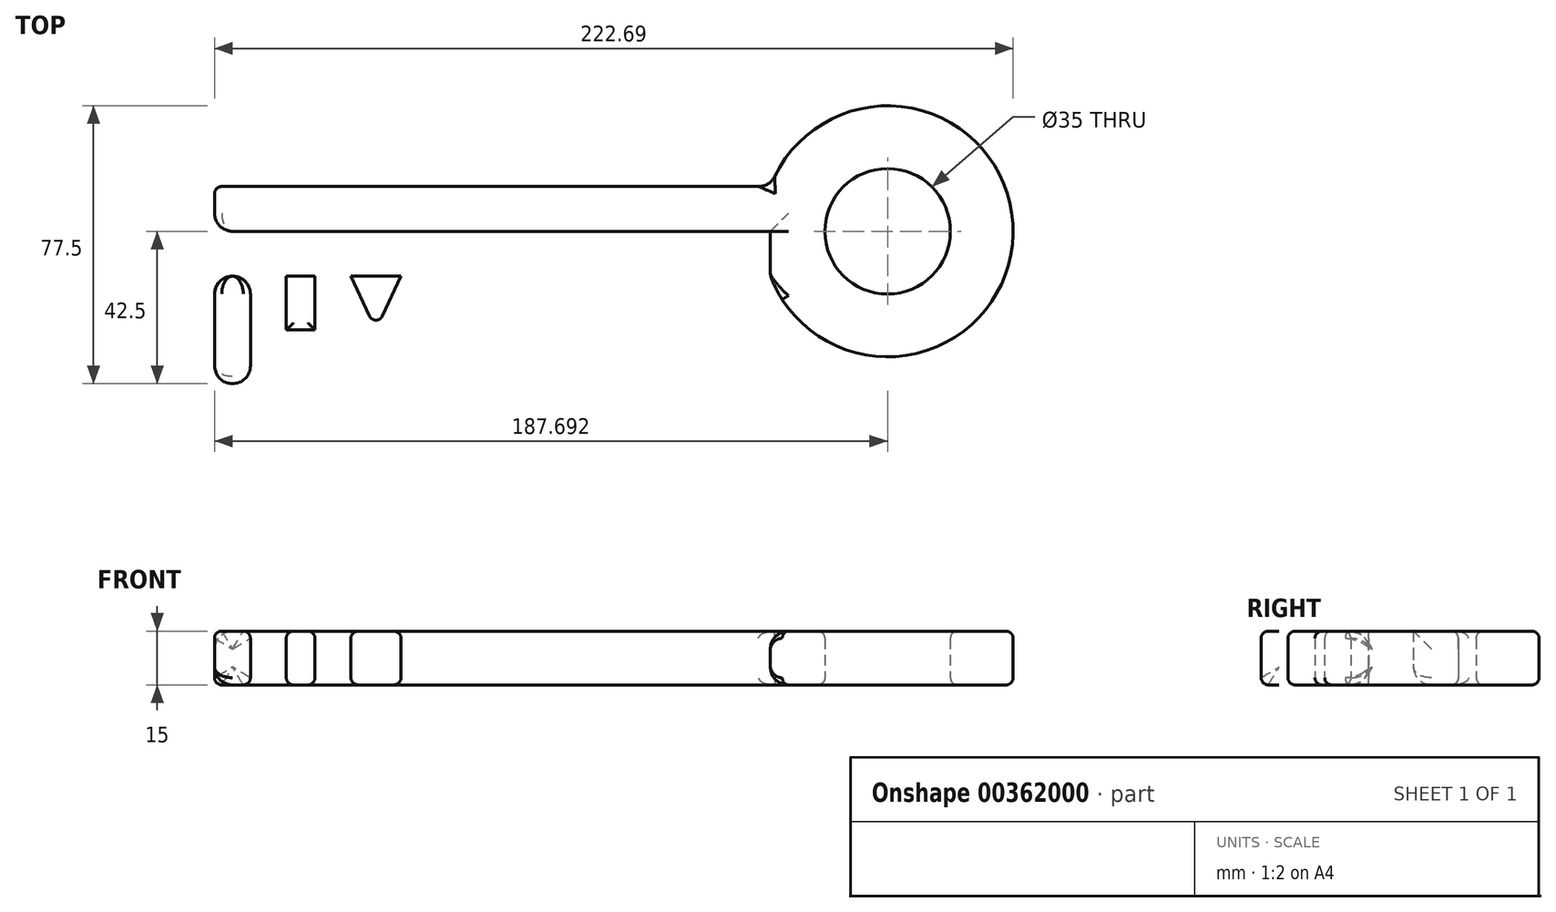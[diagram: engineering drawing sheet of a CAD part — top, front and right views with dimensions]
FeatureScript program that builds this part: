
annotation { "Feature Type Name" : "Feature", "Feature Type Description" : "" }
export const myFeature = defineFeature(function(context is Context, id is Id, definition is map)
    precondition{}
    {
        {
            var Q0;
            Q0=qCreatedBy(makeId("Top.planeOp"),FACE);
            var sketch = newSketch(context, id + "F0", { "sketchPlane" : qUnion([Q0])});
            skLineSegment(sketch, "E0.bottom", {"start": v(-105.84, 55) * mm, "end": v(49.16, 55) * mm});
            skLineSegment(sketch, "E0.top", {"start": v(-105.84, 30) * mm, "end": v(49.16, 30) * mm});
            skLineSegment(sketch, "E0.left", {"start": v(-105.84, 55) * mm, "end": v(-105.84, 30) * mm});
            skLineSegment(sketch, "E0.right", {"start": v(49.16, 55) * mm, "end": v(49.16, 30) * mm});
            skLineSegment(sketch, "E1.bottom", {"start": v(50.65, 30) * mm, "end": v(-105.84, 30) * mm});
            skLineSegment(sketch, "E1.top", {"start": v(50.65, 30) * mm, "end": v(-105.84, 30) * mm});
            skLineSegment(sketch, "E1.left", {"start": v(50.65, 30) * mm, "end": v(50.65, 30) * mm});
            skLineSegment(sketch, "E1.right", {"start": v(-105.84, 30) * mm, "end": v(-105.84, 30) * mm});
            skLineSegment(sketch, "E2.bottom", {"start": v(-105.84, 0) * mm, "end": v(-95.84, 0) * mm});
            skLineSegment(sketch, "E2.top", {"start": v(-105.84, 30) * mm, "end": v(-95.84, 30) * mm});
            skLineSegment(sketch, "E2.left", {"start": v(-105.84, 0) * mm, "end": v(-105.84, 30) * mm});
            skLineSegment(sketch, "E2.right", {"start": v(-95.84, 0) * mm, "end": v(-95.84, 30) * mm});
            skPoint(sketch, "E3.firstSnap0", {"position": v(-95.84, 15) * mm});
            skLineSegment(sketch, "E3.bottom", {"start": v(-85.84, 15) * mm, "end": v(-77.84, 15) * mm});
            skLineSegment(sketch, "E3.top", {"start": v(-85.84, 30) * mm, "end": v(-77.84, 30) * mm});
            skLineSegment(sketch, "E3.left", {"start": v(-85.84, 15) * mm, "end": v(-85.84, 30) * mm});
            skLineSegment(sketch, "E3.right", {"start": v(-77.84, 15) * mm, "end": v(-77.84, 30) * mm});
            skLineSegment(sketch, "E4", {"start": v(-67.84, 30) * mm, "end": v(-60.84, 15) * mm});
            skLineSegment(sketch, "E5", {"start": v(-60.84, 15) * mm, "end": v(-53.84, 30) * mm});
            skArc(sketch, "E6", {"start": v(49.16, 30) * mm, "mid": v(116.85, 42.5) * mm, "end": v(49.16, 55) * mm});
            skCircle(sketch, "E7", {"center": v(81.85, 42.5) * mm, "radius": 17.5 * mm});
            skLineSegment(sketch, "E8", {"start": v(81.85, 42.5) * mm, "end": v(-105.84, 42.5) * mm});
            skLineSegment(sketch, "E9", {"start": v(33.31, 42.5) * mm, "end": v(-105.84, 42.5) * mm});
            skSolve(sketch);
        }
        {
            var Q0;
            {var subQ0=sQuery(id+"F0.wireOp",EDGE,"E4");Q0=makeQuery(id+"F0.imprint","IMPRINT",FACE,{"disambiguationData":[TD([[makeQuery(id+"F0.imprint","IMPRINT",EDGE,{"derivedFrom":subQ0}),1.0]])]});}
            var Q1;
            Q1=makeQuery(id+"F0.imprint","IMPRINT",FACE,{"disambiguationData":[TD([[makeQuery(id+"F0.imprint","IMPRINT",EDGE,{"derivedFrom":sQuery(id+"F0.wireOp",EDGE,"E2.bottom")}),1.0]])]});
            var Q2;
            Q2=makeQuery(id+"F0.imprint","IMPRINT",FACE,{"disambiguationData":[TD([[makeQuery(id+"F0.imprint","IMPRINT",EDGE,{"derivedFrom":sQuery(id+"F0.wireOp",EDGE,"E3.bottom")}),1.0]])]});
            var Q3;
            {var subQ0=sQuery(id+"F0.wireOp",EDGE,"E6");Q3=makeQuery(id+"F0.imprint","IMPRINT",FACE,{"disambiguationData":[TD([[makeQuery(id+"F0.imprint","IMPRINT",EDGE,{"derivedFrom":subQ0}),1.0]])]});}
            var Q4;
            {var subQ7=sQuery(id+"F0.wireOp",EDGE,"E3.top");Q4=makeQuery(id+"F0.imprint","IMPRINT",FACE,{"disambiguationData":[TD([[makeQuery(id+"F0.imprint","IMPRINT",EDGE,{"derivedFrom":subQ7}),1.0]])]});}
            var Q5;
            {var subQ4=sQuery(id+"F0.wireOp",EDGE,"E0.bottom");Q5=makeQuery(id+"F0.imprint","IMPRINT",FACE,{"disambiguationData":[TD([[makeQuery(id+"F0.imprint","IMPRINT",EDGE,{"derivedFrom":subQ4}),-1.0]])]});}
            extrude(context, id + "F1", {"entities" : qUnion([Q0, Q1, Q2, Q3, Q4, Q5]), "depth" : 15 * mm});
        }
        {
            var Q0;
            Q0=makeQuery(id+"F1.opExtrude","CAP_EDGE",EDGE,{"disambiguationData":[OSD([sQuery(id+"F0.wireOp",EDGE,"E0.bottom")])],"isStart":false});
            var Q1;
            Q1=makeQuery(id+"F1.opExtrude","CAP_EDGE",EDGE,{"disambiguationData":[OSD([sQuery(id+"F0.wireOp",EDGE,"E2.bottom")])],"isStart":false});
            var Q2;
            Q2=makeQuery(id+"F1.opExtrude","CAP_EDGE",EDGE,{"disambiguationData":[OSD([sQuery(id+"F0.wireOp",EDGE,"E2.left")])],"isStart":false});
            var Q3;
            {var subQ0=sQuery(id+"F0.wireOp",EDGE,"E1.top");Q3=makeQuery(id+"F1.opExtrude","CAP_EDGE",EDGE,{"disambiguationData":[OSD([subQ0]),TDD([makeQuery(id+"F0.imprint","IMPRINT",EDGE,{"disambiguationData":[TD([[makeQuery(id+"F0.imprint","INTERSECT",VERTEX,{"derivedFrom":[subQ0,sQuery(id+"F0.wireOp",EDGE,"E2.top"),sQuery(id+"F0.wireOp",EDGE,"E2.right")]}),1.0]])],"derivedFrom":subQ0})])],"isStart":false});}
            var Q4;
            Q4=makeQuery(id+"F1.opExtrude","CAP_EDGE",EDGE,{"disambiguationData":[OSD([sQuery(id+"F0.wireOp",EDGE,"E2.right")])],"isStart":false});
            var Q5;
            Q5=makeQuery(id+"F1.opExtrude","CAP_EDGE",EDGE,{"disambiguationData":[OSD([sQuery(id+"F0.wireOp",EDGE,"E3.left")])],"isStart":false});
            var Q6;
            Q6=makeQuery(id+"F1.opExtrude","CAP_EDGE",EDGE,{"disambiguationData":[OSD([sQuery(id+"F0.wireOp",EDGE,"E3.bottom")])],"isStart":false});
            var Q7;
            Q7=makeQuery(id+"F1.opExtrude","CAP_EDGE",EDGE,{"disambiguationData":[OSD([sQuery(id+"F0.wireOp",EDGE,"E3.right")])],"isStart":false});
            var Q8;
            {var subQ0=sQuery(id+"F0.wireOp",EDGE,"E1.top");Q8=makeQuery(id+"F1.opExtrude","CAP_EDGE",EDGE,{"disambiguationData":[OSD([subQ0]),TDD([makeQuery(id+"F0.imprint","IMPRINT",EDGE,{"disambiguationData":[TD([[makeQuery(id+"F0.imprint","INTERSECT",VERTEX,{"derivedFrom":[subQ0,sQuery(id+"F0.wireOp",EDGE,"E4")]}),-1.0]])],"derivedFrom":subQ0})])],"isStart":false});}
            var Q9;
            Q9=makeQuery(id+"F1.opExtrude","CAP_EDGE",EDGE,{"disambiguationData":[OSD([sQuery(id+"F0.wireOp",EDGE,"E4")])],"isStart":false});
            var Q10;
            {var subQ0=sQuery(id+"F0.wireOp",EDGE,"E1.top");Q10=makeQuery(id+"F1.opExtrude","CAP_EDGE",EDGE,{"disambiguationData":[OSD([subQ0]),TDD([makeQuery(id+"F0.imprint","IMPRINT",EDGE,{"disambiguationData":[TD([[makeQuery(id+"F0.imprint","INTERSECT",VERTEX,{"derivedFrom":[subQ0,sQuery(id+"F0.wireOp",EDGE,"E5")]}),1.0]])],"derivedFrom":subQ0})])],"isStart":false});}
            var Q11;
            Q11=makeQuery(id+"F1.opExtrude","CAP_EDGE",EDGE,{"disambiguationData":[OSD([sQuery(id+"F0.wireOp",EDGE,"E6")])],"isStart":false});
            var Q12;
            Q12=makeQuery(id+"F1.opExtrude","CAP_EDGE",EDGE,{"disambiguationData":[OSD([sQuery(id+"F0.wireOp",EDGE,"E7")])],"isStart":false});
            var Q13;
            Q13=makeQuery(id+"F1.opExtrude","CAP_EDGE",EDGE,{"disambiguationData":[OSD([sQuery(id+"F0.wireOp",EDGE,"E5")])],"isStart":true});
            var Q14;
            Q14=makeQuery(id+"F1.opExtrude","CAP_EDGE",EDGE,{"disambiguationData":[OSD([sQuery(id+"F0.wireOp",EDGE,"E0.left")])],"isStart":true});
            var Q15;
            Q15=makeQuery(id+"F1.opExtrude","CAP_EDGE",EDGE,{"disambiguationData":[OSD([sQuery(id+"F0.wireOp",EDGE,"E6")])],"isStart":true});
            var Q16;
            {var subQ0=sQuery(id+"F0.wireOp",EDGE,"E1.top");Q16=makeQuery(id+"F1.opExtrude","CAP_EDGE",EDGE,{"disambiguationData":[OSD([subQ0]),TDD([makeQuery(id+"F0.imprint","IMPRINT",EDGE,{"disambiguationData":[TD([[makeQuery(id+"F0.imprint","INTERSECT",VERTEX,{"derivedFrom":[subQ0,sQuery(id+"F0.wireOp",EDGE,"E5")]}),1.0]])],"derivedFrom":subQ0})])],"isStart":true});}
            var Q17;
            Q17=makeQuery(id+"F1.opExtrude","CAP_EDGE",EDGE,{"disambiguationData":[OSD([sQuery(id+"F0.wireOp",EDGE,"E3.bottom")])],"isStart":true});
            var Q18;
            Q18=makeQuery(id+"F1.opExtrude","CAP_EDGE",EDGE,{"disambiguationData":[OSD([sQuery(id+"F0.wireOp",EDGE,"E3.right")])],"isStart":true});
            var Q19;
            Q19=makeQuery(id+"F1.opExtrude","CAP_EDGE",EDGE,{"disambiguationData":[OSD([sQuery(id+"F0.wireOp",EDGE,"E2.right")])],"isStart":true});
            var Q20;
            Q20=makeQuery(id+"F1.opExtrude","CAP_EDGE",EDGE,{"disambiguationData":[OSD([sQuery(id+"F0.wireOp",EDGE,"E2.bottom")])],"isStart":true});
            var Q21;
            Q21=makeQuery(id+"F1.opExtrude","CAP_EDGE",EDGE,{"disambiguationData":[OSD([sQuery(id+"F0.wireOp",EDGE,"E7")])],"isStart":true});
            var Q22;
            Q22=makeQuery(id+"F1.opExtrude","CAP_EDGE",EDGE,{"disambiguationData":[OSD([sQuery(id+"F0.wireOp",EDGE,"E0.bottom")])],"isStart":true});
            var Q23;
            Q23=makeQuery(id+"F1.opExtrude","SWEPT_EDGE",EDGE,{"disambiguationData":[OSD([sQuery(id+"F0.wireOp",EDGE,"E0.bottom"),sQuery(id+"F0.wireOp",EDGE,"E0.left")])]});
            var Q24;
            Q24=makeQuery(id+"F1.opExtrude","CAP_EDGE",EDGE,{"disambiguationData":[OSD([sQuery(id+"F0.wireOp",EDGE,"E4")])],"isStart":true});
            var Q25;
            Q25=makeQuery(id+"F1.opExtrude","SWEPT_EDGE",EDGE,{"disambiguationData":[OSD([sQuery(id+"F0.wireOp",EDGE,"E4"),sQuery(id+"F0.wireOp",EDGE,"E5")])]});
            var Q26;
            Q26=makeQuery(id+"F1.opExtrude","CAP_EDGE",EDGE,{"disambiguationData":[OSD([sQuery(id+"F0.wireOp",EDGE,"E5")])],"isStart":false});
            var Q27;
            {var subQ0=sQuery(id+"F0.wireOp",EDGE,"E1.top");Q27=makeQuery(id+"F1.opExtrude","CAP_EDGE",EDGE,{"disambiguationData":[OSD([subQ0]),TDD([makeQuery(id+"F0.imprint","IMPRINT",EDGE,{"disambiguationData":[TD([[makeQuery(id+"F0.imprint","INTERSECT",VERTEX,{"derivedFrom":[subQ0,sQuery(id+"F0.wireOp",EDGE,"E2.top"),sQuery(id+"F0.wireOp",EDGE,"E2.right")]}),1.0]])],"derivedFrom":subQ0})])],"isStart":true});}
            var Q28;
            Q28=makeQuery(id+"F1.opExtrude","CAP_EDGE",EDGE,{"disambiguationData":[OSD([sQuery(id+"F0.wireOp",EDGE,"E3.left")])],"isStart":true});
            var Q29;
            {var subQ0=sQuery(id+"F0.wireOp",EDGE,"E1.top");Q29=makeQuery(id+"F1.opExtrude","CAP_EDGE",EDGE,{"disambiguationData":[OSD([subQ0]),TDD([makeQuery(id+"F0.imprint","IMPRINT",EDGE,{"disambiguationData":[TD([[makeQuery(id+"F0.imprint","INTERSECT",VERTEX,{"derivedFrom":[subQ0,sQuery(id+"F0.wireOp",EDGE,"E4")]}),-1.0]])],"derivedFrom":subQ0})])],"isStart":true});}
            fillet(context, id + "F2", {"entities" : qUnion([Q0, Q1, Q2, Q3, Q4, Q5, Q6, Q7, Q8, Q9, Q10, Q11, Q12, Q13, Q14, Q15, Q16, Q17, Q18, Q19, Q20, Q21, Q22, Q23, Q24, Q25, Q26, Q27, Q28, Q29]), "radius" : 2 * mm, "tangentPropagation" : true, "allowEdgeOverflow" : false});
        }
        {
            var Q0;
            Q0=makeQuery(id+"F1.opExtrude","CAP_EDGE",EDGE,{"disambiguationData":[OSD([sQuery(id+"F0.wireOp",EDGE,"E2.left")])],"isStart":true});
            var Q1;
            Q1=makeQuery(id+"F1.opExtrude","CAP_EDGE",EDGE,{"disambiguationData":[OSD([sQuery(id+"F0.wireOp",EDGE,"E2.right")])],"isStart":true});
            var Q2;
            {var subQ0=sQuery(id+"F0.wireOp",EDGE,"E1.top");Q2=makeQuery(id+"F1.opExtrude","CAP_EDGE",EDGE,{"disambiguationData":[OSD([subQ0]),TDD([makeQuery(id+"F0.imprint","IMPRINT",EDGE,{"disambiguationData":[TD([[makeQuery(id+"F0.imprint","INTERSECT",VERTEX,{"derivedFrom":[subQ0,sQuery(id+"F0.wireOp",EDGE,"E2.top"),sQuery(id+"F0.wireOp",EDGE,"E2.right")]}),1.0]])],"derivedFrom":subQ0})])],"isStart":true});}
            var Q3;
            Q3=makeQuery(id+"F1.opExtrude","CAP_EDGE",EDGE,{"disambiguationData":[OSD([sQuery(id+"F0.wireOp",EDGE,"E3.left")])],"isStart":true});
            var Q4;
            Q4=makeQuery(id+"F1.opExtrude","CAP_EDGE",EDGE,{"disambiguationData":[OSD([sQuery(id+"F0.wireOp",EDGE,"E3.bottom")])],"isStart":true});
            var Q5;
            Q5=makeQuery(id+"F1.opExtrude","CAP_EDGE",EDGE,{"disambiguationData":[OSD([sQuery(id+"F0.wireOp",EDGE,"E3.right")])],"isStart":true});
            var Q6;
            Q6=makeQuery(id+"F1.opExtrude","CAP_EDGE",EDGE,{"disambiguationData":[OSD([sQuery(id+"F0.wireOp",EDGE,"E2.bottom")])],"isStart":true});
            var Q7;
            {var subQ0=sQuery(id+"F0.wireOp",EDGE,"E1.top");Q7=makeQuery(id+"F1.opExtrude","CAP_EDGE",EDGE,{"disambiguationData":[OSD([subQ0]),TDD([makeQuery(id+"F0.imprint","IMPRINT",EDGE,{"disambiguationData":[TD([[makeQuery(id+"F0.imprint","INTERSECT",VERTEX,{"derivedFrom":[subQ0,sQuery(id+"F0.wireOp",EDGE,"E4")]}),-1.0]])],"derivedFrom":subQ0})])],"isStart":true});}
            var Q8;
            Q8=makeQuery(id+"F1.opExtrude","CAP_EDGE",EDGE,{"disambiguationData":[OSD([sQuery(id+"F0.wireOp",EDGE,"E4")])],"isStart":true});
            var Q9;
            {var subQ0=sQuery(id+"F0.wireOp",EDGE,"E1.top");Q9=makeQuery(id+"F1.opExtrude","CAP_EDGE",EDGE,{"disambiguationData":[OSD([subQ0]),TDD([makeQuery(id+"F0.imprint","IMPRINT",EDGE,{"disambiguationData":[TD([[makeQuery(id+"F0.imprint","INTERSECT",VERTEX,{"derivedFrom":[subQ0,sQuery(id+"F0.wireOp",EDGE,"E5")]}),1.0]])],"derivedFrom":subQ0})])],"isStart":true});}
            var Q10;
            {var subQ0=sQuery(id+"F0.wireOp",EDGE,"E5");Q10=makeQuery(id+"F2.opFillet","BLEND_EDGE",EDGE,{"blendedFrom":[makeQuery(id+"F1.opExtrude","CAP_EDGE",EDGE,{"disambiguationData":[OSD([subQ0])],"isStart":true}),makeQuery(id+"F1.opExtrude","CAP_FACE",FACE,{"disambiguationData":[OSD([sQuery(id+"F0.wireOp",EDGE,"E0.bottom"),sQuery(id+"F0.wireOp",EDGE,"E0.left"),sQuery(id+"F0.wireOp",EDGE,"E1.top"),sQuery(id+"F0.wireOp",EDGE,"E2.bottom"),sQuery(id+"F0.wireOp",EDGE,"E2.top"),sQuery(id+"F0.wireOp",EDGE,"E2.left"),sQuery(id+"F0.wireOp",EDGE,"E2.right"),sQuery(id+"F0.wireOp",EDGE,"E3.bottom"),sQuery(id+"F0.wireOp",EDGE,"E3.left"),sQuery(id+"F0.wireOp",EDGE,"E3.right"),sQuery(id+"F0.wireOp",EDGE,"E4"),subQ0,sQuery(id+"F0.wireOp",EDGE,"E6"),sQuery(id+"F0.wireOp",EDGE,"E7")])],"isStart":true})],"blendedInto":[makeQuery(id+"F1.opExtrude","CAP_FACE",FACE,{"disambiguationData":[OSD([sQuery(id+"F0.wireOp",EDGE,"E0.bottom"),sQuery(id+"F0.wireOp",EDGE,"E0.left"),sQuery(id+"F0.wireOp",EDGE,"E1.top"),sQuery(id+"F0.wireOp",EDGE,"E2.bottom"),sQuery(id+"F0.wireOp",EDGE,"E2.top"),sQuery(id+"F0.wireOp",EDGE,"E2.left"),sQuery(id+"F0.wireOp",EDGE,"E2.right"),sQuery(id+"F0.wireOp",EDGE,"E3.bottom"),sQuery(id+"F0.wireOp",EDGE,"E3.left"),sQuery(id+"F0.wireOp",EDGE,"E3.right"),sQuery(id+"F0.wireOp",EDGE,"E4"),subQ0,sQuery(id+"F0.wireOp",EDGE,"E6"),sQuery(id+"F0.wireOp",EDGE,"E7")])],"isStart":true})]});}
            var Q11;
            Q11=makeQuery(id+"F1.opExtrude","CAP_EDGE",EDGE,{"disambiguationData":[OSD([sQuery(id+"F0.wireOp",EDGE,"E6")])],"isStart":true});
            var Q12;
            Q12=makeQuery(id+"F1.opExtrude","CAP_EDGE",EDGE,{"disambiguationData":[OSD([sQuery(id+"F0.wireOp",EDGE,"E7")])],"isStart":true});
            var Q13;
            Q13=makeQuery(id+"F1.opExtrude","CAP_EDGE",EDGE,{"disambiguationData":[OSD([sQuery(id+"F0.wireOp",EDGE,"E0.bottom")])],"isStart":true});
            var Q14;
            Q14=makeQuery(id+"F1.opExtrude","CAP_FACE",FACE,{"disambiguationData":[OSD([sQuery(id+"F0.wireOp",EDGE,"E0.bottom"),sQuery(id+"F0.wireOp",EDGE,"E0.left"),sQuery(id+"F0.wireOp",EDGE,"E1.top"),sQuery(id+"F0.wireOp",EDGE,"E2.bottom"),sQuery(id+"F0.wireOp",EDGE,"E2.top"),sQuery(id+"F0.wireOp",EDGE,"E2.left"),sQuery(id+"F0.wireOp",EDGE,"E2.right"),sQuery(id+"F0.wireOp",EDGE,"E3.bottom"),sQuery(id+"F0.wireOp",EDGE,"E3.left"),sQuery(id+"F0.wireOp",EDGE,"E3.right"),sQuery(id+"F0.wireOp",EDGE,"E4"),sQuery(id+"F0.wireOp",EDGE,"E5"),sQuery(id+"F0.wireOp",EDGE,"E6"),sQuery(id+"F0.wireOp",EDGE,"E7")])],"isStart":true});
            var Q15;
            {var subQ0=sQuery(id+"F0.wireOp",EDGE,"E0.left");Q15=makeQuery(id+"F2.opFillet","BLEND_EDGE",EDGE,{"blendedFrom":[makeQuery(id+"F1.opExtrude","CAP_EDGE",EDGE,{"disambiguationData":[OSD([subQ0])],"isStart":true}),makeQuery(id+"F1.opExtrude","SWEPT_FACE",FACE,{"disambiguationData":[OSD([subQ0])]})],"blendedInto":[makeQuery(id+"F1.opExtrude","SWEPT_FACE",FACE,{"disambiguationData":[OSD([subQ0])]})]});}
            var Q16;
            Q16=makeQuery(id+"F1.opExtrude","SWEPT_FACE",FACE,{"disambiguationData":[OSD([sQuery(id+"F0.wireOp",EDGE,"E0.left")])]});
            var Q17;
            {var subQ0=sQuery(id+"F0.wireOp",EDGE,"E2.left");Q17=makeQuery(id+"F2.opFillet","BLEND_EDGE",EDGE,{"blendedFrom":[makeQuery(id+"F1.opExtrude","CAP_EDGE",EDGE,{"disambiguationData":[OSD([subQ0])],"isStart":false}),makeQuery(id+"F1.opExtrude","CAP_FACE",FACE,{"disambiguationData":[OSD([sQuery(id+"F0.wireOp",EDGE,"E0.bottom"),sQuery(id+"F0.wireOp",EDGE,"E0.left"),sQuery(id+"F0.wireOp",EDGE,"E1.top"),sQuery(id+"F0.wireOp",EDGE,"E2.bottom"),subQ0,sQuery(id+"F0.wireOp",EDGE,"E2.right"),sQuery(id+"F0.wireOp",EDGE,"E3.bottom"),sQuery(id+"F0.wireOp",EDGE,"E3.left"),sQuery(id+"F0.wireOp",EDGE,"E3.right"),sQuery(id+"F0.wireOp",EDGE,"E4"),sQuery(id+"F0.wireOp",EDGE,"E5"),sQuery(id+"F0.wireOp",EDGE,"E6"),sQuery(id+"F0.wireOp",EDGE,"E7")])],"isStart":false})],"blendedInto":[makeQuery(id+"F1.opExtrude","CAP_FACE",FACE,{"disambiguationData":[OSD([sQuery(id+"F0.wireOp",EDGE,"E0.bottom"),sQuery(id+"F0.wireOp",EDGE,"E0.left"),sQuery(id+"F0.wireOp",EDGE,"E1.top"),sQuery(id+"F0.wireOp",EDGE,"E2.bottom"),subQ0,sQuery(id+"F0.wireOp",EDGE,"E2.right"),sQuery(id+"F0.wireOp",EDGE,"E3.bottom"),sQuery(id+"F0.wireOp",EDGE,"E3.left"),sQuery(id+"F0.wireOp",EDGE,"E3.right"),sQuery(id+"F0.wireOp",EDGE,"E4"),sQuery(id+"F0.wireOp",EDGE,"E5"),sQuery(id+"F0.wireOp",EDGE,"E6"),sQuery(id+"F0.wireOp",EDGE,"E7")])],"isStart":false})]});}
            var Q18;
            {var subQ0=sQuery(id+"F0.wireOp",EDGE,"E2.left");Q18=makeQuery(id+"F2.opFillet","BLEND_EDGE",EDGE,{"blendedFrom":[makeQuery(id+"F1.opExtrude","CAP_EDGE",EDGE,{"disambiguationData":[OSD([subQ0])],"isStart":false}),makeQuery(id+"F1.opExtrude","SWEPT_FACE",FACE,{"disambiguationData":[OSD([subQ0])]})],"blendedInto":[makeQuery(id+"F1.opExtrude","SWEPT_FACE",FACE,{"disambiguationData":[OSD([subQ0])]})]});}
            var Q19;
            Q19=makeQuery(id+"F2.opFillet","BLEND_EDGE",EDGE,{"blendedFrom":[makeQuery(id+"F1.opExtrude","CAP_EDGE",EDGE,{"disambiguationData":[OSD([sQuery(id+"F0.wireOp",EDGE,"E0.bottom")])],"isStart":false}),makeQuery(id+"F1.opExtrude","CAP_EDGE",EDGE,{"disambiguationData":[OSD([sQuery(id+"F0.wireOp",EDGE,"E0.left"),sQuery(id+"F0.wireOp",EDGE,"E2.left")])],"isStart":false})],"blendedInto":[]});
            var Q20;
            {var subQ0=sQuery(id+"F0.wireOp",EDGE,"E4");Q20=makeQuery(id+"F2.opFillet","BLEND_EDGE",EDGE,{"blendedFrom":[makeQuery(id+"F1.opExtrude","CAP_EDGE",EDGE,{"disambiguationData":[OSD([subQ0])],"isStart":false}),makeQuery(id+"F1.opExtrude","SWEPT_FACE",FACE,{"disambiguationData":[OSD([subQ0])]})],"blendedInto":[makeQuery(id+"F1.opExtrude","SWEPT_FACE",FACE,{"disambiguationData":[OSD([subQ0])]})]});}
            var Q21;
            Q21=makeQuery(id+"F2.opFillet","BLEND_EDGE",EDGE,{"blendedFrom":[makeQuery(id+"F1.opExtrude","CAP_EDGE",EDGE,{"disambiguationData":[OSD([sQuery(id+"F0.wireOp",EDGE,"E4")])],"isStart":false}),makeQuery(id+"F1.opExtrude","SWEPT_FACE",FACE,{"disambiguationData":[OSD([sQuery(id+"F0.wireOp",EDGE,"E5")])]})],"blendedInto":[makeQuery(id+"F1.opExtrude","SWEPT_FACE",FACE,{"disambiguationData":[OSD([sQuery(id+"F0.wireOp",EDGE,"E5")])]})]});
            var Q22;
            Q22=makeQuery(id+"F2.opFillet","BLEND_EDGE",EDGE,{"blendedFrom":[makeQuery(id+"F1.opExtrude","CAP_EDGE",EDGE,{"disambiguationData":[OSD([sQuery(id+"F0.wireOp",EDGE,"E3.bottom")])],"isStart":false}),makeQuery(id+"F1.opExtrude","CAP_EDGE",EDGE,{"disambiguationData":[OSD([sQuery(id+"F0.wireOp",EDGE,"E3.right")])],"isStart":false})],"blendedInto":[]});
            var Q23;
            {var subQ0=sQuery(id+"F0.wireOp",EDGE,"E3.right");var subQ1=sQuery(id+"F0.wireOp",EDGE,"E1.top");Q23=makeQuery(id+"F2.opFillet","BLEND_EDGE",EDGE,{"blendedFrom":[makeQuery(id+"F1.opExtrude","CAP_EDGE",EDGE,{"disambiguationData":[OSD([subQ1]),TDD([makeQuery(id+"F0.imprint","IMPRINT",EDGE,{"disambiguationData":[TD([[makeQuery(id+"F0.imprint","INTERSECT",VERTEX,{"derivedFrom":[subQ1,sQuery(id+"F0.wireOp",EDGE,"E4")]}),-1.0]])],"derivedFrom":subQ1})])],"isStart":false}),makeQuery(id+"F1.opExtrude","CAP_EDGE",EDGE,{"disambiguationData":[OSD([subQ0])],"isStart":false})],"blendedInto":[]});}
            var Q24;
            {var subQ0=sQuery(id+"F0.wireOp",EDGE,"E4");var subQ1=sQuery(id+"F0.wireOp",EDGE,"E1.top");Q24=makeQuery(id+"F2.opFillet","BLEND_EDGE",EDGE,{"blendedFrom":[makeQuery(id+"F1.opExtrude","CAP_EDGE",EDGE,{"disambiguationData":[OSD([subQ1]),TDD([makeQuery(id+"F0.imprint","IMPRINT",EDGE,{"disambiguationData":[TD([[makeQuery(id+"F0.imprint","INTERSECT",VERTEX,{"derivedFrom":[subQ1,subQ0]}),-1.0]])],"derivedFrom":subQ1})])],"isStart":false}),makeQuery(id+"F1.opExtrude","CAP_EDGE",EDGE,{"disambiguationData":[OSD([subQ0])],"isStart":false})],"blendedInto":[]});}
            var Q25;
            {var subQ0=sQuery(id+"F0.wireOp",EDGE,"E3.left");var subQ1=sQuery(id+"F0.wireOp",EDGE,"E1.top");Q25=makeQuery(id+"F2.opFillet","BLEND_EDGE",EDGE,{"blendedFrom":[makeQuery(id+"F1.opExtrude","CAP_EDGE",EDGE,{"disambiguationData":[OSD([subQ1]),TDD([makeQuery(id+"F0.imprint","IMPRINT",EDGE,{"disambiguationData":[TD([[makeQuery(id+"F0.imprint","INTERSECT",VERTEX,{"derivedFrom":[subQ1,sQuery(id+"F0.wireOp",EDGE,"E2.top"),sQuery(id+"F0.wireOp",EDGE,"E2.right")]}),1.0]])],"derivedFrom":subQ1})])],"isStart":false}),makeQuery(id+"F1.opExtrude","CAP_EDGE",EDGE,{"disambiguationData":[OSD([subQ0])],"isStart":false})],"blendedInto":[]});}
            var Q26;
            {var subQ0=sQuery(id+"F0.wireOp",EDGE,"E6");Q26=makeQuery(id+"F2.opFillet","BLEND_EDGE",EDGE,{"blendedFrom":[makeQuery(id+"F1.opExtrude","CAP_EDGE",EDGE,{"disambiguationData":[OSD([subQ0])],"isStart":false}),makeQuery(id+"F1.opExtrude","CAP_FACE",FACE,{"disambiguationData":[OSD([sQuery(id+"F0.wireOp",EDGE,"E0.bottom"),sQuery(id+"F0.wireOp",EDGE,"E0.left"),sQuery(id+"F0.wireOp",EDGE,"E1.top"),sQuery(id+"F0.wireOp",EDGE,"E2.bottom"),sQuery(id+"F0.wireOp",EDGE,"E2.left"),sQuery(id+"F0.wireOp",EDGE,"E2.right"),sQuery(id+"F0.wireOp",EDGE,"E3.bottom"),sQuery(id+"F0.wireOp",EDGE,"E3.left"),sQuery(id+"F0.wireOp",EDGE,"E3.right"),sQuery(id+"F0.wireOp",EDGE,"E4"),sQuery(id+"F0.wireOp",EDGE,"E5"),subQ0,sQuery(id+"F0.wireOp",EDGE,"E7")])],"isStart":false})],"blendedInto":[makeQuery(id+"F1.opExtrude","CAP_FACE",FACE,{"disambiguationData":[OSD([sQuery(id+"F0.wireOp",EDGE,"E0.bottom"),sQuery(id+"F0.wireOp",EDGE,"E0.left"),sQuery(id+"F0.wireOp",EDGE,"E1.top"),sQuery(id+"F0.wireOp",EDGE,"E2.bottom"),sQuery(id+"F0.wireOp",EDGE,"E2.left"),sQuery(id+"F0.wireOp",EDGE,"E2.right"),sQuery(id+"F0.wireOp",EDGE,"E3.bottom"),sQuery(id+"F0.wireOp",EDGE,"E3.left"),sQuery(id+"F0.wireOp",EDGE,"E3.right"),sQuery(id+"F0.wireOp",EDGE,"E4"),sQuery(id+"F0.wireOp",EDGE,"E5"),subQ0,sQuery(id+"F0.wireOp",EDGE,"E7")])],"isStart":false})]});}
            var Q27;
            {var subQ0=sQuery(id+"F0.wireOp",EDGE,"E6");var subQ1=sQuery(id+"F0.wireOp",EDGE,"E5");var subQ2=sQuery(id+"F0.wireOp",EDGE,"E1.top");Q27=makeQuery(id+"F2.opFillet","BLEND_EDGE",EDGE,{"blendedFrom":[makeQuery(id+"F1.opExtrude","CAP_EDGE",EDGE,{"disambiguationData":[OSD([subQ2]),TDD([makeQuery(id+"F0.imprint","IMPRINT",EDGE,{"disambiguationData":[TD([[makeQuery(id+"F0.imprint","INTERSECT",VERTEX,{"derivedFrom":[subQ2,subQ1]}),1.0]])],"derivedFrom":subQ2})])],"isStart":false}),makeQuery(id+"F1.opExtrude","CAP_FACE",FACE,{"disambiguationData":[OSD([sQuery(id+"F0.wireOp",EDGE,"E0.bottom"),sQuery(id+"F0.wireOp",EDGE,"E0.left"),subQ2,sQuery(id+"F0.wireOp",EDGE,"E2.bottom"),sQuery(id+"F0.wireOp",EDGE,"E2.left"),sQuery(id+"F0.wireOp",EDGE,"E2.right"),sQuery(id+"F0.wireOp",EDGE,"E3.bottom"),sQuery(id+"F0.wireOp",EDGE,"E3.left"),sQuery(id+"F0.wireOp",EDGE,"E3.right"),sQuery(id+"F0.wireOp",EDGE,"E4"),subQ1,subQ0,sQuery(id+"F0.wireOp",EDGE,"E7")])],"isStart":false})],"blendedInto":[makeQuery(id+"F1.opExtrude","CAP_FACE",FACE,{"disambiguationData":[OSD([sQuery(id+"F0.wireOp",EDGE,"E0.bottom"),sQuery(id+"F0.wireOp",EDGE,"E0.left"),subQ2,sQuery(id+"F0.wireOp",EDGE,"E2.bottom"),sQuery(id+"F0.wireOp",EDGE,"E2.left"),sQuery(id+"F0.wireOp",EDGE,"E2.right"),sQuery(id+"F0.wireOp",EDGE,"E3.bottom"),sQuery(id+"F0.wireOp",EDGE,"E3.left"),sQuery(id+"F0.wireOp",EDGE,"E3.right"),sQuery(id+"F0.wireOp",EDGE,"E4"),subQ1,subQ0,sQuery(id+"F0.wireOp",EDGE,"E7")])],"isStart":false})]});}
            var Q28;
            Q28=makeQuery(id+"F1.opExtrude","SWEPT_EDGE",EDGE,{"disambiguationData":[OSD([sQuery(id+"F0.wireOp",EDGE,"E0.right"),sQuery(id+"F0.wireOp",EDGE,"E1.top"),sQuery(id+"F0.wireOp",EDGE,"E6")])]});
            var Q29;
            {var subQ0=sQuery(id+"F0.wireOp",EDGE,"E6");var subQ1=sQuery(id+"F0.wireOp",EDGE,"E1.top");Q29=makeQuery(id+"F2.opFillet","BLEND_EDGE",EDGE,{"blendedFrom":[makeQuery(id+"F1.opExtrude","CAP_EDGE",EDGE,{"disambiguationData":[OSD([subQ1]),TDD([makeQuery(id+"F0.imprint","IMPRINT",EDGE,{"disambiguationData":[TD([[makeQuery(id+"F0.imprint","INTERSECT",VERTEX,{"derivedFrom":[subQ1,sQuery(id+"F0.wireOp",EDGE,"E5")]}),1.0]])],"derivedFrom":subQ1})])],"isStart":false}),makeQuery(id+"F1.opExtrude","CAP_EDGE",EDGE,{"disambiguationData":[OSD([subQ0])],"isStart":false})],"blendedInto":[]});}
            var Q30;
            {var subQ0=sQuery(id+"F0.wireOp",EDGE,"E6");Q30=makeQuery(id+"F2.opFillet","BLEND_EDGE",EDGE,{"blendedFrom":[makeQuery(id+"F1.opExtrude","CAP_EDGE",EDGE,{"disambiguationData":[OSD([subQ0])],"isStart":false}),makeQuery(id+"F1.opExtrude","SWEPT_FACE",FACE,{"disambiguationData":[OSD([subQ0])]})],"blendedInto":[makeQuery(id+"F1.opExtrude","SWEPT_FACE",FACE,{"disambiguationData":[OSD([subQ0])]})]});}
            var Q31;
            Q31=makeQuery(id+"F2.opFillet","BLEND_FACE",FACE,{"disambiguationData":[OSD([sQuery(id+"F0.wireOp",EDGE,"E6")])]});
            var Q32;
            Q32=makeQuery(id+"F1.opExtrude","SWEPT_EDGE",EDGE,{"disambiguationData":[OSD([sQuery(id+"F0.wireOp",EDGE,"E4"),sQuery(id+"F0.wireOp",EDGE,"E5")])]});
            var Q33;
            Q33=makeQuery(id+"F1.opExtrude","SWEPT_EDGE",EDGE,{"disambiguationData":[OSD([sQuery(id+"F0.wireOp",EDGE,"E1.top"),sQuery(id+"F0.wireOp",EDGE,"E4")])]});
            var Q34;
            {var subQ0=sQuery(id+"F0.wireOp",EDGE,"E4");var subQ1=sQuery(id+"F0.wireOp",EDGE,"E3.right");var subQ2=sQuery(id+"F0.wireOp",EDGE,"E1.top");Q34=makeQuery(id+"F2.opFillet","BLEND_EDGE",EDGE,{"blendedFrom":[makeQuery(id+"F1.opExtrude","CAP_EDGE",EDGE,{"disambiguationData":[OSD([subQ2]),TDD([makeQuery(id+"F0.imprint","IMPRINT",EDGE,{"disambiguationData":[TD([[makeQuery(id+"F0.imprint","INTERSECT",VERTEX,{"derivedFrom":[subQ2,subQ0]}),-1.0]])],"derivedFrom":subQ2})])],"isStart":false}),makeQuery(id+"F1.opExtrude","CAP_FACE",FACE,{"disambiguationData":[OSD([sQuery(id+"F0.wireOp",EDGE,"E0.bottom"),sQuery(id+"F0.wireOp",EDGE,"E0.left"),subQ2,sQuery(id+"F0.wireOp",EDGE,"E2.bottom"),sQuery(id+"F0.wireOp",EDGE,"E2.left"),sQuery(id+"F0.wireOp",EDGE,"E2.right"),sQuery(id+"F0.wireOp",EDGE,"E3.bottom"),sQuery(id+"F0.wireOp",EDGE,"E3.left"),subQ1,subQ0,sQuery(id+"F0.wireOp",EDGE,"E5"),sQuery(id+"F0.wireOp",EDGE,"E6"),sQuery(id+"F0.wireOp",EDGE,"E7")])],"isStart":false})],"blendedInto":[makeQuery(id+"F1.opExtrude","CAP_FACE",FACE,{"disambiguationData":[OSD([sQuery(id+"F0.wireOp",EDGE,"E0.bottom"),sQuery(id+"F0.wireOp",EDGE,"E0.left"),subQ2,sQuery(id+"F0.wireOp",EDGE,"E2.bottom"),sQuery(id+"F0.wireOp",EDGE,"E2.left"),sQuery(id+"F0.wireOp",EDGE,"E2.right"),sQuery(id+"F0.wireOp",EDGE,"E3.bottom"),sQuery(id+"F0.wireOp",EDGE,"E3.left"),subQ1,subQ0,sQuery(id+"F0.wireOp",EDGE,"E5"),sQuery(id+"F0.wireOp",EDGE,"E6"),sQuery(id+"F0.wireOp",EDGE,"E7")])],"isStart":false})]});}
            var Q35;
            Q35=makeQuery(id+"F1.opExtrude","SWEPT_EDGE",EDGE,{"disambiguationData":[OSD([sQuery(id+"F0.wireOp",EDGE,"E3.bottom"),sQuery(id+"F0.wireOp",EDGE,"E3.left")])]});
            var Q36;
            Q36=makeQuery(id+"F1.opExtrude","SWEPT_EDGE",EDGE,{"disambiguationData":[OSD([sQuery(id+"F0.wireOp",EDGE,"E2.bottom"),sQuery(id+"F0.wireOp",EDGE,"E2.right")])]});
            var Q37;
            Q37=makeQuery(id+"F2.opFillet","BLEND_EDGE",EDGE,{"blendedFrom":[makeQuery(id+"F1.opExtrude","CAP_EDGE",EDGE,{"disambiguationData":[OSD([sQuery(id+"F0.wireOp",EDGE,"E2.bottom")])],"isStart":false}),makeQuery(id+"F1.opExtrude","CAP_EDGE",EDGE,{"disambiguationData":[OSD([sQuery(id+"F0.wireOp",EDGE,"E2.right")])],"isStart":false})],"blendedInto":[]});
            var Q38;
            {var subQ0=sQuery(id+"F0.wireOp",EDGE,"E3.left");var subQ1=sQuery(id+"F0.wireOp",EDGE,"E2.right");var subQ2=sQuery(id+"F0.wireOp",EDGE,"E1.top");Q38=makeQuery(id+"F2.opFillet","BLEND_EDGE",EDGE,{"blendedFrom":[makeQuery(id+"F1.opExtrude","CAP_EDGE",EDGE,{"disambiguationData":[OSD([subQ2]),TDD([makeQuery(id+"F0.imprint","IMPRINT",EDGE,{"disambiguationData":[TD([[makeQuery(id+"F0.imprint","INTERSECT",VERTEX,{"derivedFrom":[subQ2,sQuery(id+"F0.wireOp",EDGE,"E2.top"),subQ1]}),1.0]])],"derivedFrom":subQ2})])],"isStart":false}),makeQuery(id+"F1.opExtrude","CAP_FACE",FACE,{"disambiguationData":[OSD([sQuery(id+"F0.wireOp",EDGE,"E0.bottom"),sQuery(id+"F0.wireOp",EDGE,"E0.left"),subQ2,sQuery(id+"F0.wireOp",EDGE,"E2.bottom"),sQuery(id+"F0.wireOp",EDGE,"E2.left"),subQ1,sQuery(id+"F0.wireOp",EDGE,"E3.bottom"),subQ0,sQuery(id+"F0.wireOp",EDGE,"E3.right"),sQuery(id+"F0.wireOp",EDGE,"E4"),sQuery(id+"F0.wireOp",EDGE,"E5"),sQuery(id+"F0.wireOp",EDGE,"E6"),sQuery(id+"F0.wireOp",EDGE,"E7")])],"isStart":false})],"blendedInto":[makeQuery(id+"F1.opExtrude","CAP_FACE",FACE,{"disambiguationData":[OSD([sQuery(id+"F0.wireOp",EDGE,"E0.bottom"),sQuery(id+"F0.wireOp",EDGE,"E0.left"),subQ2,sQuery(id+"F0.wireOp",EDGE,"E2.bottom"),sQuery(id+"F0.wireOp",EDGE,"E2.left"),subQ1,sQuery(id+"F0.wireOp",EDGE,"E3.bottom"),subQ0,sQuery(id+"F0.wireOp",EDGE,"E3.right"),sQuery(id+"F0.wireOp",EDGE,"E4"),sQuery(id+"F0.wireOp",EDGE,"E5"),sQuery(id+"F0.wireOp",EDGE,"E6"),sQuery(id+"F0.wireOp",EDGE,"E7")])],"isStart":false})]});}
            var Q39;
            Q39=makeQuery(id+"F1.opExtrude","SWEPT_EDGE",EDGE,{"disambiguationData":[OSD([sQuery(id+"F0.wireOp",EDGE,"E3.bottom"),sQuery(id+"F0.wireOp",EDGE,"E3.right")])]});
            var Q40;
            {var subQ0=sQuery(id+"F0.wireOp",EDGE,"E3.bottom");Q40=makeQuery(id+"F2.opFillet","BLEND_EDGE",EDGE,{"blendedFrom":[makeQuery(id+"F1.opExtrude","CAP_EDGE",EDGE,{"disambiguationData":[OSD([subQ0])],"isStart":false}),makeQuery(id+"F1.opExtrude","CAP_FACE",FACE,{"disambiguationData":[OSD([sQuery(id+"F0.wireOp",EDGE,"E0.bottom"),sQuery(id+"F0.wireOp",EDGE,"E0.left"),sQuery(id+"F0.wireOp",EDGE,"E1.top"),sQuery(id+"F0.wireOp",EDGE,"E2.bottom"),sQuery(id+"F0.wireOp",EDGE,"E2.left"),sQuery(id+"F0.wireOp",EDGE,"E2.right"),subQ0,sQuery(id+"F0.wireOp",EDGE,"E3.left"),sQuery(id+"F0.wireOp",EDGE,"E3.right"),sQuery(id+"F0.wireOp",EDGE,"E4"),sQuery(id+"F0.wireOp",EDGE,"E5"),sQuery(id+"F0.wireOp",EDGE,"E6"),sQuery(id+"F0.wireOp",EDGE,"E7")])],"isStart":false})],"blendedInto":[makeQuery(id+"F1.opExtrude","CAP_FACE",FACE,{"disambiguationData":[OSD([sQuery(id+"F0.wireOp",EDGE,"E0.bottom"),sQuery(id+"F0.wireOp",EDGE,"E0.left"),sQuery(id+"F0.wireOp",EDGE,"E1.top"),sQuery(id+"F0.wireOp",EDGE,"E2.bottom"),sQuery(id+"F0.wireOp",EDGE,"E2.left"),sQuery(id+"F0.wireOp",EDGE,"E2.right"),subQ0,sQuery(id+"F0.wireOp",EDGE,"E3.left"),sQuery(id+"F0.wireOp",EDGE,"E3.right"),sQuery(id+"F0.wireOp",EDGE,"E4"),sQuery(id+"F0.wireOp",EDGE,"E5"),sQuery(id+"F0.wireOp",EDGE,"E6"),sQuery(id+"F0.wireOp",EDGE,"E7")])],"isStart":false})]});}
            var Q41;
            {var subQ0=sQuery(id+"F0.wireOp",EDGE,"E2.bottom");Q41=makeQuery(id+"F2.opFillet","BLEND_EDGE",EDGE,{"blendedFrom":[makeQuery(id+"F1.opExtrude","CAP_EDGE",EDGE,{"disambiguationData":[OSD([subQ0])],"isStart":false}),makeQuery(id+"F1.opExtrude","CAP_FACE",FACE,{"disambiguationData":[OSD([sQuery(id+"F0.wireOp",EDGE,"E0.bottom"),sQuery(id+"F0.wireOp",EDGE,"E0.left"),sQuery(id+"F0.wireOp",EDGE,"E1.top"),subQ0,sQuery(id+"F0.wireOp",EDGE,"E2.left"),sQuery(id+"F0.wireOp",EDGE,"E2.right"),sQuery(id+"F0.wireOp",EDGE,"E3.bottom"),sQuery(id+"F0.wireOp",EDGE,"E3.left"),sQuery(id+"F0.wireOp",EDGE,"E3.right"),sQuery(id+"F0.wireOp",EDGE,"E4"),sQuery(id+"F0.wireOp",EDGE,"E5"),sQuery(id+"F0.wireOp",EDGE,"E6"),sQuery(id+"F0.wireOp",EDGE,"E7")])],"isStart":false})],"blendedInto":[makeQuery(id+"F1.opExtrude","CAP_FACE",FACE,{"disambiguationData":[OSD([sQuery(id+"F0.wireOp",EDGE,"E0.bottom"),sQuery(id+"F0.wireOp",EDGE,"E0.left"),sQuery(id+"F0.wireOp",EDGE,"E1.top"),subQ0,sQuery(id+"F0.wireOp",EDGE,"E2.left"),sQuery(id+"F0.wireOp",EDGE,"E2.right"),sQuery(id+"F0.wireOp",EDGE,"E3.bottom"),sQuery(id+"F0.wireOp",EDGE,"E3.left"),sQuery(id+"F0.wireOp",EDGE,"E3.right"),sQuery(id+"F0.wireOp",EDGE,"E4"),sQuery(id+"F0.wireOp",EDGE,"E5"),sQuery(id+"F0.wireOp",EDGE,"E6"),sQuery(id+"F0.wireOp",EDGE,"E7")])],"isStart":false})]});}
            var Q42;
            {var subQ0=sQuery(id+"F0.wireOp",EDGE,"E4");Q42=makeQuery(id+"F2.opFillet","BLEND_EDGE",EDGE,{"blendedFrom":[makeQuery(id+"F1.opExtrude","CAP_EDGE",EDGE,{"disambiguationData":[OSD([subQ0])],"isStart":false}),makeQuery(id+"F1.opExtrude","CAP_FACE",FACE,{"disambiguationData":[OSD([sQuery(id+"F0.wireOp",EDGE,"E0.bottom"),sQuery(id+"F0.wireOp",EDGE,"E0.left"),sQuery(id+"F0.wireOp",EDGE,"E1.top"),sQuery(id+"F0.wireOp",EDGE,"E2.bottom"),sQuery(id+"F0.wireOp",EDGE,"E2.left"),sQuery(id+"F0.wireOp",EDGE,"E2.right"),sQuery(id+"F0.wireOp",EDGE,"E3.bottom"),sQuery(id+"F0.wireOp",EDGE,"E3.left"),sQuery(id+"F0.wireOp",EDGE,"E3.right"),subQ0,sQuery(id+"F0.wireOp",EDGE,"E5"),sQuery(id+"F0.wireOp",EDGE,"E6"),sQuery(id+"F0.wireOp",EDGE,"E7")])],"isStart":false})],"blendedInto":[makeQuery(id+"F1.opExtrude","CAP_FACE",FACE,{"disambiguationData":[OSD([sQuery(id+"F0.wireOp",EDGE,"E0.bottom"),sQuery(id+"F0.wireOp",EDGE,"E0.left"),sQuery(id+"F0.wireOp",EDGE,"E1.top"),sQuery(id+"F0.wireOp",EDGE,"E2.bottom"),sQuery(id+"F0.wireOp",EDGE,"E2.left"),sQuery(id+"F0.wireOp",EDGE,"E2.right"),sQuery(id+"F0.wireOp",EDGE,"E3.bottom"),sQuery(id+"F0.wireOp",EDGE,"E3.left"),sQuery(id+"F0.wireOp",EDGE,"E3.right"),subQ0,sQuery(id+"F0.wireOp",EDGE,"E5"),sQuery(id+"F0.wireOp",EDGE,"E6"),sQuery(id+"F0.wireOp",EDGE,"E7")])],"isStart":false})]});}
            var Q43;
            {var subQ0=sQuery(id+"F0.wireOp",EDGE,"E5");Q43=makeQuery(id+"F2.opFillet","BLEND_EDGE",EDGE,{"blendedFrom":[makeQuery(id+"F1.opExtrude","CAP_EDGE",EDGE,{"disambiguationData":[OSD([subQ0])],"isStart":true}),makeQuery(id+"F1.opExtrude","SWEPT_FACE",FACE,{"disambiguationData":[OSD([subQ0])]})],"blendedInto":[makeQuery(id+"F1.opExtrude","SWEPT_FACE",FACE,{"disambiguationData":[OSD([subQ0])]})]});}
            var Q44;
            Q44=makeQuery(id+"F2.opFillet","BLEND_EDGE",EDGE,{"blendedFrom":[makeQuery(id+"F1.opExtrude","CAP_EDGE",EDGE,{"disambiguationData":[OSD([sQuery(id+"F0.wireOp",EDGE,"E5")])],"isStart":true}),makeQuery(id+"F1.opExtrude","SWEPT_FACE",FACE,{"disambiguationData":[OSD([sQuery(id+"F0.wireOp",EDGE,"E4")])]})],"blendedInto":[makeQuery(id+"F1.opExtrude","SWEPT_FACE",FACE,{"disambiguationData":[OSD([sQuery(id+"F0.wireOp",EDGE,"E4")])]})]});
            var Q45;
            {var subQ0=sQuery(id+"F0.wireOp",EDGE,"E1.top");var subQ1=sQuery(id+"F0.wireOp",EDGE,"E5");Q45=makeQuery(id+"F2.opFillet","BLEND_EDGE",EDGE,{"blendedFrom":[makeQuery(id+"F1.opExtrude","CAP_EDGE",EDGE,{"disambiguationData":[OSD([subQ1])],"isStart":true}),makeQuery(id+"F1.opExtrude","SWEPT_FACE",FACE,{"disambiguationData":[OSD([subQ0]),TDD([makeQuery(id+"F0.imprint","IMPRINT",EDGE,{"disambiguationData":[TD([[makeQuery(id+"F0.imprint","INTERSECT",VERTEX,{"derivedFrom":[subQ0,subQ1]}),1.0]])],"derivedFrom":subQ0})])]})],"blendedInto":[makeQuery(id+"F1.opExtrude","SWEPT_FACE",FACE,{"disambiguationData":[OSD([subQ0]),TDD([makeQuery(id+"F0.imprint","IMPRINT",EDGE,{"disambiguationData":[TD([[makeQuery(id+"F0.imprint","INTERSECT",VERTEX,{"derivedFrom":[subQ0,subQ1]}),1.0]])],"derivedFrom":subQ0})])]})]});}
            var Q46;
            Q46=makeQuery(id+"F1.opExtrude","SWEPT_EDGE",EDGE,{"disambiguationData":[OSD([sQuery(id+"F0.wireOp",EDGE,"E1.top"),sQuery(id+"F0.wireOp",EDGE,"E5")])]});
            var Q47;
            {var subQ0=sQuery(id+"F0.wireOp",EDGE,"E0.bottom");Q47=makeQuery(id+"F2.opFillet","BLEND_EDGE",EDGE,{"blendedFrom":[makeQuery(id+"F1.opExtrude","CAP_EDGE",EDGE,{"disambiguationData":[OSD([subQ0])],"isStart":false}),makeQuery(id+"F1.opExtrude","SWEPT_FACE",FACE,{"disambiguationData":[OSD([subQ0])]})],"blendedInto":[makeQuery(id+"F1.opExtrude","SWEPT_FACE",FACE,{"disambiguationData":[OSD([subQ0])]})]});}
            fillet(context, id + "F3", {"entities" : qUnion([Q0, Q1, Q2, Q3, Q4, Q5, Q6, Q7, Q8, Q9, Q10, Q11, Q12, Q13, Q14, Q15, Q16, Q17, Q18, Q19, Q20, Q21, Q22, Q23, Q24, Q25, Q26, Q27, Q28, Q29, Q30, Q31, Q32, Q33, Q34, Q35, Q36, Q37, Q38, Q39, Q40, Q41, Q42, Q43, Q44, Q45, Q46, Q47]), "radius" : 5 * mm, "tangentPropagation" : true, "allowEdgeOverflow" : false});
        }
    });
